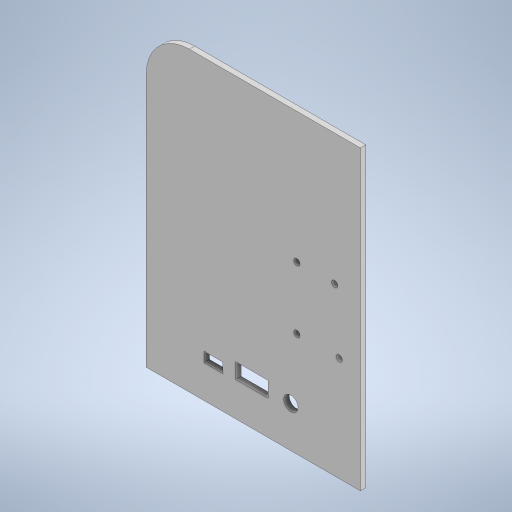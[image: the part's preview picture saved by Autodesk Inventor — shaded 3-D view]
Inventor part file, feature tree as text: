
AUTODESK INVENTOR PART (.ipt)
format: ipt  version: 2023 (Build 270158000, 158)  size: 268,288 bytes
history: native  units: in
note: dims shown in document units (in); Inventor stores cm internally (conversion verified against a paired STEP export)
features: extrude x2, sketch x2, projected_geometry x1
ambient origin geometry x8: Origin, YZ Plane, XZ Plane, XY Plane, X Axis, Y Axis, Z Axis, Center Point
bodies: Solid1 (feature_tree)
feature tree (5):
  extrude  "Extrusion1"  Depth=0.9449in
  extrude  "Extrusion2"  Depth=0.1181in TaperAngle=0.0deg
  sketch  "Sketch1"  dims[d0=4.685in d1=0.9449in]
  sketch  "Sketch2"  dims[d2=6.4961in d3=0.1181in d4=0.0in d49=0.0in d50=0.0in d51=0.0394in d52=0.5906in d53=0.0591in d54=0.0591in d55=0.0591in d56=0.0591in d57=0.0591in d58=0.0591in d59=0.0591in d60=0.0591in d63=0.1378in d64=0.315in d72=5.4713in d73=5.6898in d74=5.7165in d75=5.561in d76=2.0771in d77=3.006in d78=3.4194in d82=2.6676in d96=4.2146in d97=0.4626in d98=2.8563in d99=0.561in d102=2.8563in d103=1.3878in d104=4.2146in d105=1.3878in d106=1.5195in d107=5.5028in d108=5.5515in d109=2.1086in d110=2.184in d111=2.3546in d112=2.6361in d113=5.5028in d114=5.6002in d115=5.6437in d116=5.672in d117=3.0887in d118=3.1096in d119=3.2126in d120=3.3367in d121=5.6437in d122=5.672in]
  projected_geometry  "Projected Loop1"
